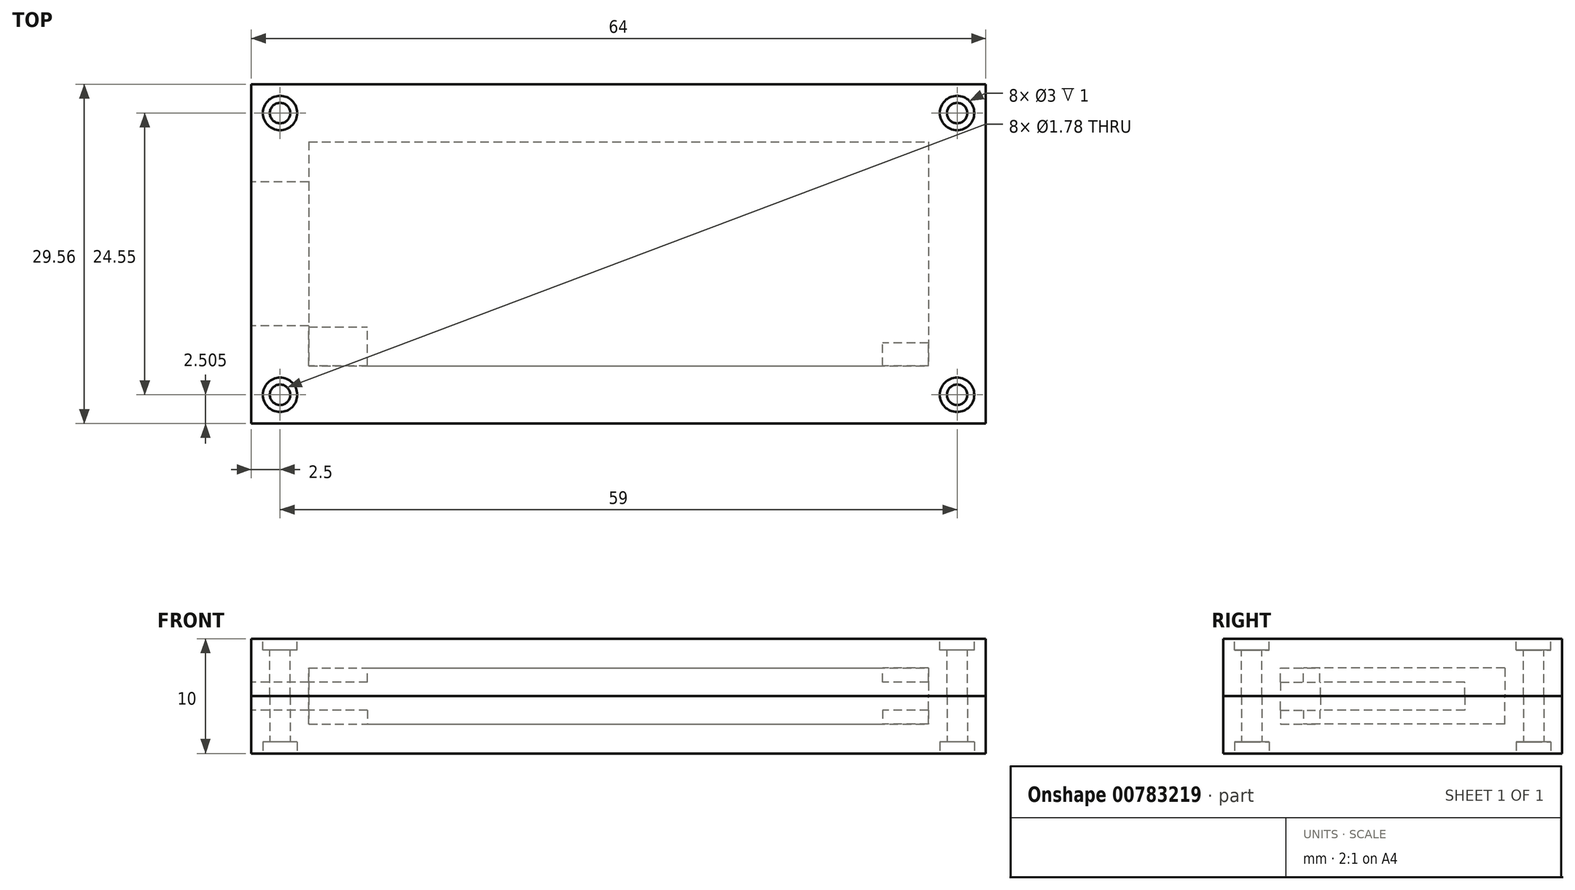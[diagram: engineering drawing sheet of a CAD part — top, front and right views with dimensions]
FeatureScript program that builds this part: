
annotation { "Feature Type Name" : "Feature", "Feature Type Description" : "" }
export const myFeature = defineFeature(function(context is Context, id is Id, definition is map)
    precondition{}
    {
        {
            var Q0;
            Q0=qCreatedBy(makeId("Top.planeOp"),FACE);
            var sketch = newSketch(context, id + "F0", { "sketchPlane" : qUnion([Q0])});
            skLineSegment(sketch, "E0.bottom", {"start": v(-27, 9.77) * mm, "end": v(27, 9.77) * mm});
            skLineSegment(sketch, "E0.top", {"start": v(-27, -9.77) * mm, "end": v(27, -9.77) * mm});
            skLineSegment(sketch, "E0.left", {"start": v(-27, 9.77) * mm, "end": v(-27, -9.77) * mm});
            skLineSegment(sketch, "E0.right", {"start": v(27, 9.77) * mm, "end": v(27, -9.77) * mm});
            skPoint(sketch, "E0.middle", {"position": v(0, 0) * mm});
            skSolve(sketch);
        }
        {
            var Q0;
            Q0=qCreatedBy(makeId("Top.planeOp"),FACE);
            var sketch = newSketch(context, id + "F1", { "sketchPlane" : qUnion([Q0])});
            skLineSegment(sketch, "E1.0", {"start": v(-32, 14.77) * mm, "end": v(-32, -14.77) * mm});
            skLineSegment(sketch, "E1.1", {"start": v(32, 14.77) * mm, "end": v(-32, 14.77) * mm});
            skLineSegment(sketch, "E1.2", {"start": v(32, -14.77) * mm, "end": v(32, 14.77) * mm});
            skLineSegment(sketch, "E1.3", {"start": v(-32, -14.77) * mm, "end": v(32, -14.77) * mm});
            skSolve(sketch);
        }
        {
            var Q0;
            Q0 = qSketchRegion(id + "F1", true);
            extrude(context, id + "F2", {"entities" : qUnion([Q0]), "depth" : 5 * mm, "offsetDistance" : 25 * mm});
        }
        {
            var Q0;
            Q0 = qSketchRegion(id + "F0", true);
            var Q1;
            Q1=makeQuery(id+"F2.opExtrude","CAP_FACE",FACE,{"disambiguationData":[OSD([sQuery(id+"F1.wireOp",EDGE,"E1.0"),sQuery(id+"F1.wireOp",EDGE,"E1.1"),sQuery(id+"F1.wireOp",EDGE,"E1.2"),sQuery(id+"F1.wireOp",EDGE,"E1.3")])],"isStart":false});
            extrude(context, id + "F3", {"entities" : qUnion([Q0]), "operationType" : NewBodyOperationType.REMOVE, "endBound" : BoundingType.UP_TO_SURFACE, "depth" : 25 * mm, "endBoundEntityFace" : qUnion([Q1]), "hasOffset" : true, "offsetDistance" : 2.55 * mm});
        }
        {
            var Q0;
            Q0=makeQuery(id+"F3.boolean.opBoolean","COPY",FACE,{"derivedFrom":makeQuery(id+"F3.opExtrude","CAP_FACE",FACE,{"disambiguationData":[OSD([sQuery(id+"F0.wireOp",EDGE,"E0.bottom"),sQuery(id+"F0.wireOp",EDGE,"E0.top"),sQuery(id+"F0.wireOp",EDGE,"E0.left"),sQuery(id+"F0.wireOp",EDGE,"E0.right")])],"isStart":false})});
            var sketch = newSketch(context, id + "F4", { "sketchPlane" : qUnion([Q0])});
            skPoint(sketch, "E2.0", {"position": v(-27, 9.77) * mm});
            skPoint(sketch, "E2.1", {"position": v(-27, -9.77) * mm});
            skLineSegment(sketch, "E3.0", {"start": v(-32, -14.77) * mm, "end": v(-32, 14.77) * mm, "construction": true});
            skLineSegment(sketch, "E4", {"start": v(-27, 6.27) * mm, "end": v(-32, 6.27) * mm, "construction": true});
            skLineSegment(sketch, "E5", {"start": v(-32, 6.27) * mm, "end": v(-32, 0) * mm});
            skLineSegment(sketch, "E6", {"start": v(-32, -6.28) * mm, "end": v(-27, -6.27) * mm, "construction": true});
            skLineSegment(sketch, "E7.bottom", {"start": v(-32, 6.27) * mm, "end": v(-27, 6.27) * mm});
            skLineSegment(sketch, "E7.top", {"start": v(-32, -6.27) * mm, "end": v(-27, -6.27) * mm});
            skLineSegment(sketch, "E7.left", {"start": v(-32, 6.27) * mm, "end": v(-32, -6.27) * mm});
            skLineSegment(sketch, "E7.right", {"start": v(-27, 6.27) * mm, "end": v(-27, -6.27) * mm});
            skSolve(sketch);
        }
        {
            var Q0;
            Q0 = qSketchRegion(id + "F4", true);
            extrude(context, id + "F5", {"entities" : qUnion([Q0]), "operationType" : NewBodyOperationType.REMOVE, "endBound" : BoundingType.THROUGH_ALL, "depth" : 25 * mm, "offsetDistance" : 25 * mm});
        }
        {
            var Q0;
            Q0=makeQuery(id+"F2.opExtrude","CAP_FACE",FACE,{"disambiguationData":[OSD([sQuery(id+"F1.wireOp",EDGE,"E1.0"),sQuery(id+"F1.wireOp",EDGE,"E1.1"),sQuery(id+"F1.wireOp",EDGE,"E1.2"),sQuery(id+"F1.wireOp",EDGE,"E1.3")])],"isStart":false});
            var sketch = newSketch(context, id + "F6", { "sketchPlane" : qUnion([Q0])});
            skPoint(sketch, "E8.0", {"position": v(-27, 9.77) * mm});
            skPoint(sketch, "E8.1", {"position": v(27, 9.77) * mm});
            skPoint(sketch, "E8.2", {"position": v(27, -9.77) * mm});
            skPoint(sketch, "E8.3", {"position": v(32, -14.77) * mm});
            skPoint(sketch, "E8.4", {"position": v(32, 14.77) * mm});
            skPoint(sketch, "E8.5", {"position": v(-32, 14.77) * mm});
            skPoint(sketch, "E8.6", {"position": v(-32, -14.77) * mm});
            skPoint(sketch, "E8.7", {"position": v(-27, -9.77) * mm});
            skLineSegment(sketch, "E9", {"start": v(-32, 14.78) * mm, "end": v(-27, 9.77) * mm, "construction": true});
            skLineSegment(sketch, "E10", {"start": v(32, 14.77) * mm, "end": v(27, 9.77) * mm, "construction": true});
            skLineSegment(sketch, "E11", {"start": v(27, -9.77) * mm, "end": v(32, -14.77) * mm, "construction": true});
            skLineSegment(sketch, "E12", {"start": v(-27, -9.77) * mm, "end": v(-32, -14.77) * mm, "construction": true});
            skPoint(sketch, "E13", {"position": v(-29.5, 12.27) * mm});
            skPoint(sketch, "E14", {"position": v(29.5, 12.27) * mm});
            skPoint(sketch, "E15", {"position": v(29.5, -12.27) * mm});
            skPoint(sketch, "E16", {"position": v(-29.5, -12.27) * mm});
            skCircle(sketch, "E17", {"center": v(-29.5, -12.27) * mm, "radius": 1.5 * mm});
            skCircle(sketch, "E18", {"center": v(-29.5, 12.27) * mm, "radius": 1.5 * mm});
            skCircle(sketch, "E19", {"center": v(29.5, 12.27) * mm, "radius": 1.5 * mm});
            skCircle(sketch, "E20", {"center": v(29.5, -12.27) * mm, "radius": 1.5 * mm});
            skSolve(sketch);
        }
        {
            var Q0;
            Q0 = qSketchRegion(id + "F6", true);
            extrude(context, id + "F7", {"entities" : qUnion([Q0]), "operationType" : NewBodyOperationType.REMOVE, "oppositeDirection" : true, "depth" : 1 * mm, "offsetDistance" : 25 * mm});
        }
        {
            var Q0;
            Q0=sQuery(id+"F6.wireOp",VERTEX,"E13");
            var Q1;
            Q1=sQuery(id+"F6.wireOp",VERTEX,"E16");
            var Q2;
            Q2=sQuery(id+"F6.wireOp",VERTEX,"E14");
            var Q3;
            Q3=sQuery(id+"F6.wireOp",VERTEX,"E15");
            var Q4;
            Q4=makeQuery(id+"F2.opExtrude","SWEPT_BODY",BODY,{"disambiguationData":[OSD([sQuery(id+"F1.wireOp",EDGE,"E1.0"),sQuery(id+"F1.wireOp",EDGE,"E1.1"),sQuery(id+"F1.wireOp",EDGE,"E1.2"),sQuery(id+"F1.wireOp",EDGE,"E1.3")])]});
            hole(context, id + "F8", {"style" : HoleStyle.SIMPLE, "endStyle" : HoleEndStyle.THROUGH, "standardTappedOrClearance" : lookupTablePath({ "standard" : "ANSI", "engagement" : "75%", "pitch" : "56 tpi", "size" : "#2", "type" : "Tapped" }), "standardBlindInLast" : lookupTablePath({ "standard" : "ANSI", "engagement" : "75%", "pitch" : "56 tpi", "size" : "#2", "type" : "Tapped" }), "holeDiameter" : 1.78 * mm, "majorDiameter" : 2.18 * mm, "showTappedDepth" : true, "isTappedThrough" : true, "tappedDepth" : 12 * mm, "tapClearance" : 3, "locations" : qUnion([Q0, Q1, Q2, Q3]), "scope" : qUnion([Q4])});
        }
        {
            var Q0;
            Q0=makeQuery(id+"F5.boolean.opBoolean","MERGE",FACE,{"derivedFrom":[makeQuery(id+"F3.boolean.opBoolean","COPY",FACE,{"derivedFrom":makeQuery(id+"F3.opExtrude","CAP_FACE",FACE,{"disambiguationData":[OSD([sQuery(id+"F0.wireOp",EDGE,"E0.bottom"),sQuery(id+"F0.wireOp",EDGE,"E0.top"),sQuery(id+"F0.wireOp",EDGE,"E0.left"),sQuery(id+"F0.wireOp",EDGE,"E0.right")])],"isStart":false})})],"fromTools":[makeQuery(id+"F5.opExtrude","CAP_FACE",FACE,{"disambiguationData":[OSD([sQuery(id+"F4.wireOp",EDGE,"E7.bottom"),sQuery(id+"F4.wireOp",EDGE,"E7.top"),sQuery(id+"F4.wireOp",EDGE,"E7.left"),sQuery(id+"F4.wireOp",EDGE,"E7.right")])],"isStart":true})]});
            var sketch = newSketch(context, id + "F9", { "sketchPlane" : qUnion([Q0])});
            skLineSegment(sketch, "E21.bottom", {"start": v(-27, 9.77) * mm, "end": v(-21.88, 9.77) * mm});
            skLineSegment(sketch, "E21.top", {"start": v(-27, 6.36) * mm, "end": v(-21.88, 6.36) * mm});
            skLineSegment(sketch, "E21.left", {"start": v(-27, 9.77) * mm, "end": v(-27, 6.36) * mm});
            skLineSegment(sketch, "E21.right", {"start": v(-21.88, 9.77) * mm, "end": v(-21.88, 6.36) * mm});
            skLineSegment(sketch, "E22.bottom", {"start": v(-27, 6.27) * mm, "end": v(-32, 6.27) * mm});
            skLineSegment(sketch, "E22.top", {"start": v(-27, -6.27) * mm, "end": v(-32, -6.27) * mm});
            skLineSegment(sketch, "E22.left", {"start": v(-27, 6.27) * mm, "end": v(-27, -6.27) * mm});
            skLineSegment(sketch, "E22.right", {"start": v(-32, 6.27) * mm, "end": v(-32, -6.27) * mm});
            skLineSegment(sketch, "E23.bottom", {"start": v(27, 9.77) * mm, "end": v(23, 9.77) * mm});
            skLineSegment(sketch, "E23.top", {"start": v(27, 7.77) * mm, "end": v(23, 7.77) * mm});
            skLineSegment(sketch, "E23.left", {"start": v(27, 9.77) * mm, "end": v(27, 7.77) * mm});
            skLineSegment(sketch, "E23.right", {"start": v(23, 9.77) * mm, "end": v(23, 7.77) * mm});
            skSolve(sketch);
        }
        {
            var Q0;
            Q0 = qSketchRegion(id + "F9", true);
            var Q1;
            Q1=makeQuery(id+"F2.opExtrude","CAP_FACE",FACE,{"disambiguationData":[OSD([sQuery(id+"F1.wireOp",EDGE,"E1.0"),sQuery(id+"F1.wireOp",EDGE,"E1.1"),sQuery(id+"F1.wireOp",EDGE,"E1.2"),sQuery(id+"F1.wireOp",EDGE,"E1.3")])],"isStart":true});
            extrude(context, id + "F10", {"entities" : qUnion([Q0]), "operationType" : NewBodyOperationType.ADD, "endBound" : BoundingType.UP_TO_SURFACE, "depth" : 25 * mm, "endBoundEntityFace" : qUnion([Q1]), "hasOffset" : true, "offsetDistance" : 1.23 * mm});
        }
        {
            var Q0;
            Q0=makeQuery(id+"F2.opExtrude","SWEPT_BODY",BODY,{"disambiguationData":[OSD([sQuery(id+"F1.wireOp",EDGE,"E1.0"),sQuery(id+"F1.wireOp",EDGE,"E1.1"),sQuery(id+"F1.wireOp",EDGE,"E1.2"),sQuery(id+"F1.wireOp",EDGE,"E1.3")])]});
            var Q1;
            Q1=qCreatedBy(makeId("Top.planeOp"),FACE);
            mirror(context, id + "F11", {"entities" : qUnion([Q0]), "mirrorPlane" : qUnion([Q1])});
        }
    });
